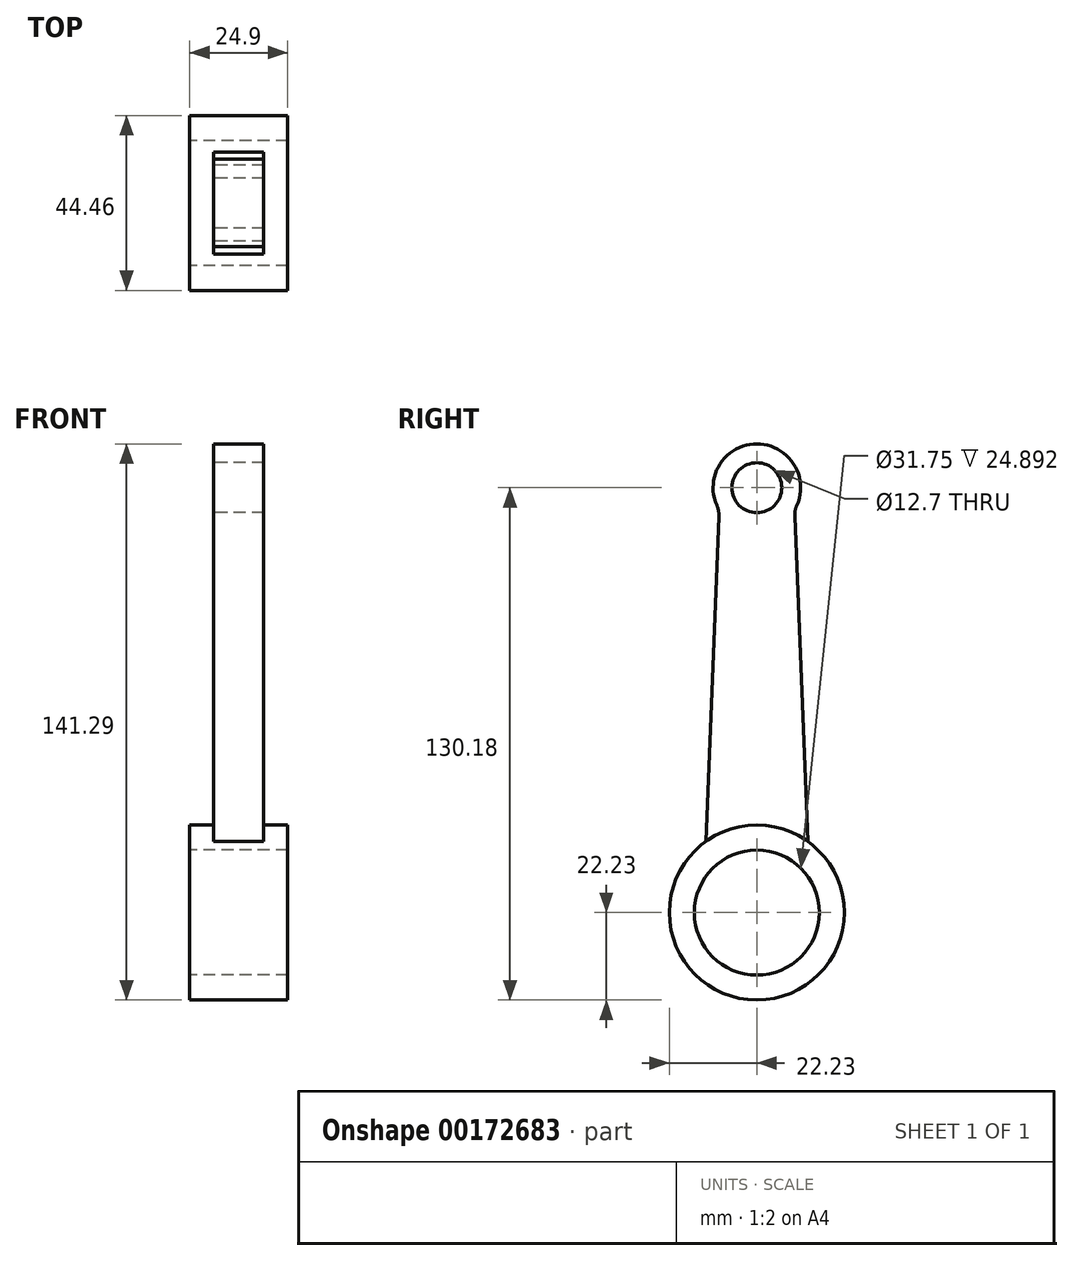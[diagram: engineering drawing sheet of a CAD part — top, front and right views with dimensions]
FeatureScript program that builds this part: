
annotation { "Feature Type Name" : "Feature", "Feature Type Description" : "" }
export const myFeature = defineFeature(function(context is Context, id is Id, definition is map)
    precondition{}
    {
        {
            var Q0;
            Q0=qCreatedBy(makeId("Right.planeOp"),FACE);
            var sketch = newSketch(context, id + "F0", { "sketchPlane" : qUnion([Q0])});
            skLineSegment(sketch, "E0", {"start": v(0, 0) * mm, "end": v(0, 107.95) * mm, "construction": true});
            skCircle(sketch, "E1", {"center": v(0, 0) * mm, "radius": 22.23 * mm});
            skCircle(sketch, "E2", {"center": v(0, 0) * mm, "radius": 15.88 * mm});
            skCircle(sketch, "E3", {"center": v(0, 107.95) * mm, "radius": 11.11 * mm});
            skCircle(sketch, "E4", {"center": v(0, 107.95) * mm, "radius": 6.35 * mm});
            skLineSegment(sketch, "E5", {"start": v(9.58, 102.32) * mm, "end": v(12.93, 18.08) * mm});
            skLineSegment(sketch, "E6", {"start": v(-9.58, 102.32) * mm, "end": v(-12.93, 18.08) * mm});
            skSolve(sketch);
        }
        {
            var Q0;
            Q0=makeQuery(id+"F0.imprint","IMPRINT",FACE,{"disambiguationData":[TD([[makeQuery(id+"F0.imprint","IMPRINT",EDGE,{"derivedFrom":sQuery(id+"F0.wireOp",EDGE,"E2")}),-1.0]])]});
            extrude(context, id + "F1", {"entities" : qUnion([Q0]), "endBound" : BoundingType.SYMMETRIC, "depth" : 24.9 * mm});
        }
        {
            var Q0;
            Q0 = qSketchRegion(id + "F0", true);
            extrude(context, id + "F2", {"entities" : qUnion([Q0]), "operationType" : NewBodyOperationType.ADD, "endBound" : BoundingType.SYMMETRIC, "depth" : 12.7 * mm});
        }
        {
            var Q0;
            Q0=makeQuery(id+"F2.opExtrude","SWEPT_EDGE",EDGE,{"disambiguationData":[OSD([sQuery(id+"F0.wireOp",EDGE,"E3"),sQuery(id+"F0.wireOp",EDGE,"E6")])]});
            var Q1;
            Q1=makeQuery(id+"F2.opExtrude","SWEPT_EDGE",EDGE,{"disambiguationData":[OSD([sQuery(id+"F0.wireOp",EDGE,"E3"),sQuery(id+"F0.wireOp",EDGE,"E5")])]});
            var Q2;
            Q2=makeQuery(id+"F2.opExtrude","SWEPT_EDGE",EDGE,{"disambiguationData":[OSD([sQuery(id+"F0.wireOp",EDGE,"E1"),sQuery(id+"F0.wireOp",EDGE,"E5")])]});
            var Q3;
            Q3=makeQuery(id+"F2.opExtrude","SWEPT_EDGE",EDGE,{"disambiguationData":[OSD([sQuery(id+"F0.wireOp",EDGE,"E1"),sQuery(id+"F0.wireOp",EDGE,"E6")])]});
            fillet(context, id + "F3", {"entities" : qUnion([Q0, Q1, Q2, Q3]), "radius" : 6.35 * mm, "tangentPropagation" : true, "allowEdgeOverflow" : false});
        }
    });
